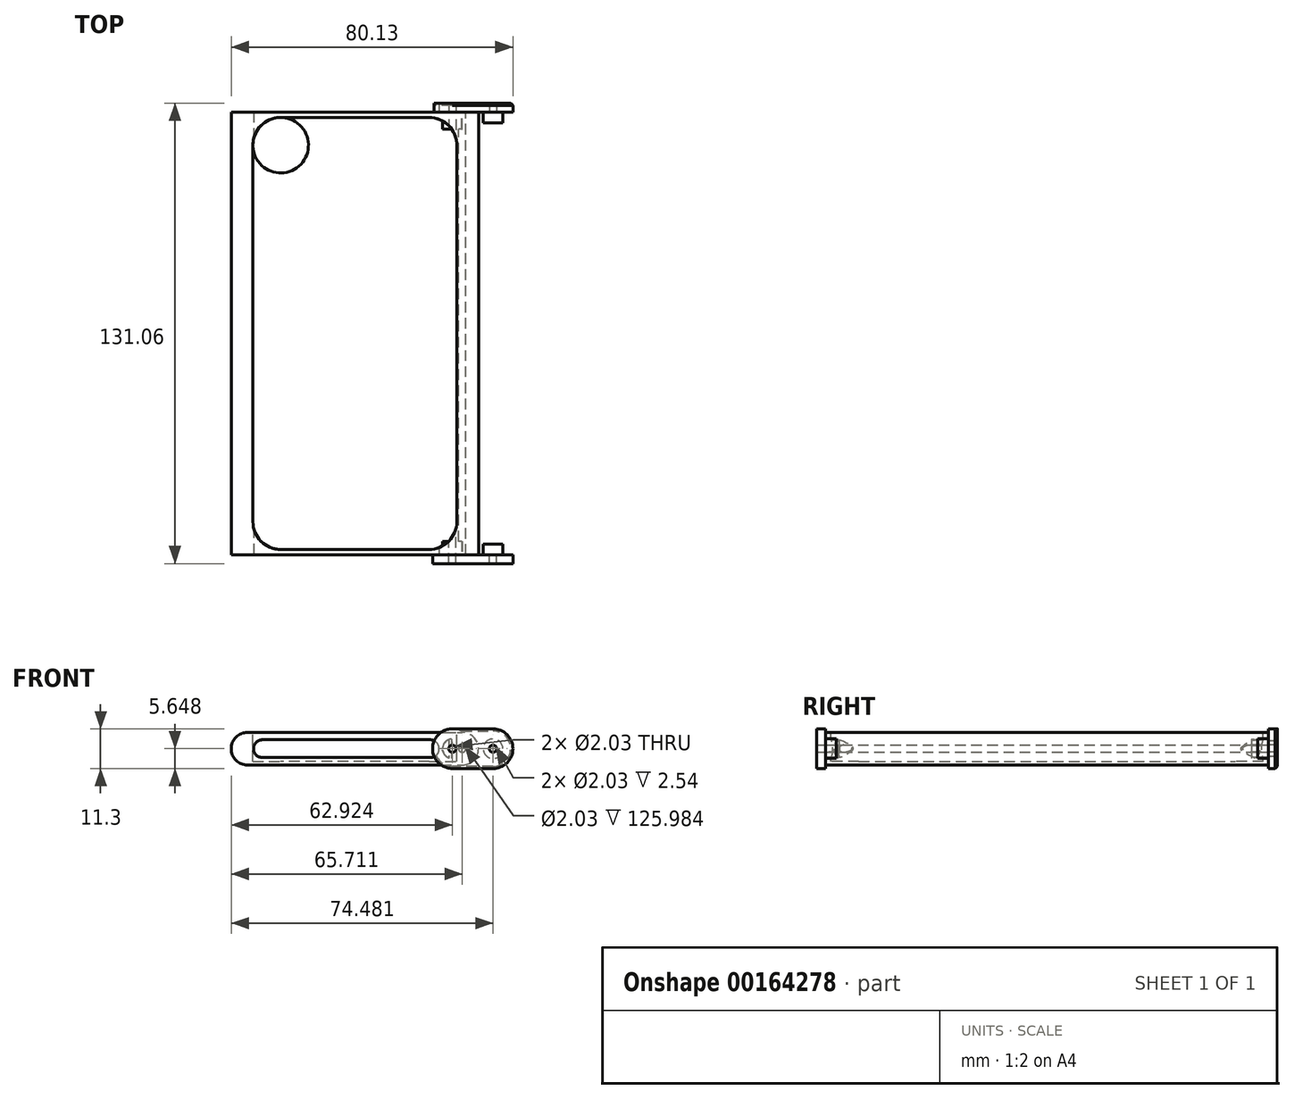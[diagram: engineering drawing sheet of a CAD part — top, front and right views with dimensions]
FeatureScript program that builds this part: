
annotation { "Feature Type Name" : "Feature", "Feature Type Description" : "" }
export const myFeature = defineFeature(function(context is Context, id is Id, definition is map)
    precondition{}
    {
        {
            var Q0;
            Q0=qCreatedBy(makeId("Top.planeOp"),FACE);
            var sketch = newSketch(context, id + "F0", { "sketchPlane" : qUnion([Q0])});
            skLineSegment(sketch, "E0.bottom", {"start": v(-35.18, 63) * mm, "end": v(35.18, 63) * mm});
            skLineSegment(sketch, "E0.top", {"start": v(-35.18, -63) * mm, "end": v(35.18, -63) * mm});
            skLineSegment(sketch, "E0.left", {"start": v(-35.18, 63) * mm, "end": v(-35.18, -63) * mm});
            skLineSegment(sketch, "E0.right", {"start": v(35.18, 63) * mm, "end": v(35.18, -63) * mm});
            skSolve(sketch);
        }
        {
            var Q0;
            Q0 = qSketchRegion(id + "F0", true);
            extrude(context, id + "F1", {"entities" : qUnion([Q0]), "depth" : 9.3 * mm});
        }
        {
            var Q0;
            Q0=makeQuery(id+"F1.opExtrude","CAP_FACE",FACE,{"disambiguationData":[OSD([sQuery(id+"F0.wireOp",EDGE,"E0.bottom"),sQuery(id+"F0.wireOp",EDGE,"E0.top"),sQuery(id+"F0.wireOp",EDGE,"E0.left"),sQuery(id+"F0.wireOp",EDGE,"E0.right")])],"isStart":false});
            var sketch = newSketch(context, id + "F2", { "sketchPlane" : qUnion([Q0])});
            skLineSegment(sketch, "E1.0", {"start": v(29, 61.47) * mm, "end": v(-29, 61.47) * mm});
            skLineSegment(sketch, "E1.1", {"start": v(29, -61.47) * mm, "end": v(29, 61.47) * mm});
            skLineSegment(sketch, "E1.2", {"start": v(-29, -61.47) * mm, "end": v(29, -61.47) * mm});
            skLineSegment(sketch, "E1.3", {"start": v(-29, 61.47) * mm, "end": v(-29, -61.47) * mm});
            skSolve(sketch);
        }
        {
            var Q0;
            Q0 = qSketchRegion(id + "F2", true);
            extrude(context, id + "F3", {"entities" : qUnion([Q0]), "operationType" : NewBodyOperationType.REMOVE, "oppositeDirection" : true, "depth" : 8.28 * mm});
        }
        {
            var Q0;
            Q0=makeQuery(id+"F3.boolean.opBoolean","COPY",EDGE,{"derivedFrom":makeQuery(id+"F3.opExtrude","SWEPT_EDGE",EDGE,{"disambiguationData":[OSD([sQuery(id+"F2.wireOp",EDGE,"E1.0"),sQuery(id+"F2.wireOp",EDGE,"E1.1")])]})});
            var Q1;
            Q1=makeQuery(id+"F3.boolean.opBoolean","COPY",EDGE,{"derivedFrom":makeQuery(id+"F3.opExtrude","SWEPT_EDGE",EDGE,{"disambiguationData":[OSD([sQuery(id+"F2.wireOp",EDGE,"E1.0"),sQuery(id+"F2.wireOp",EDGE,"E1.3")])]})});
            var Q2;
            Q2=makeQuery(id+"F3.boolean.opBoolean","COPY",EDGE,{"derivedFrom":makeQuery(id+"F3.opExtrude","SWEPT_EDGE",EDGE,{"disambiguationData":[OSD([sQuery(id+"F2.wireOp",EDGE,"E1.1"),sQuery(id+"F2.wireOp",EDGE,"E1.2")])]})});
            var Q3;
            Q3=makeQuery(id+"F3.boolean.opBoolean","COPY",EDGE,{"derivedFrom":makeQuery(id+"F3.opExtrude","SWEPT_EDGE",EDGE,{"disambiguationData":[OSD([sQuery(id+"F2.wireOp",EDGE,"E1.2"),sQuery(id+"F2.wireOp",EDGE,"E1.3")])]})});
            fillet(context, id + "F4", {"entities" : qUnion([Q0, Q1, Q2, Q3]), "radius" : 7.9 * mm, "tangentPropagation" : true, "allowEdgeOverflow" : false});
        }
        {
            var Q0;
            Q0=makeQuery(id+"F1.opExtrude","CAP_EDGE",EDGE,{"disambiguationData":[OSD([sQuery(id+"F0.wireOp",EDGE,"E0.left")])],"isStart":true});
            var Q1;
            Q1=makeQuery(id+"F1.opExtrude","CAP_EDGE",EDGE,{"disambiguationData":[OSD([sQuery(id+"F0.wireOp",EDGE,"E0.left")])],"isStart":false});
            var Q2;
            Q2=makeQuery(id+"F1.opExtrude","CAP_EDGE",EDGE,{"disambiguationData":[OSD([sQuery(id+"F0.wireOp",EDGE,"E0.right")])],"isStart":false});
            var Q3;
            Q3=makeQuery(id+"F1.opExtrude","CAP_EDGE",EDGE,{"disambiguationData":[OSD([sQuery(id+"F0.wireOp",EDGE,"E0.right")])],"isStart":true});
            fillet(context, id + "F5", {"entities" : qUnion([Q0, Q1, Q2, Q3]), "radius" : 4.65 * mm, "tangentPropagation" : true, "allowEdgeOverflow" : false});
        }
        {
            var Q0;
            Q0=makeQuery(id+"F1.opExtrude","SWEPT_FACE",FACE,{"disambiguationData":[OSD([sQuery(id+"F0.wireOp",EDGE,"E0.bottom")])]});
            var sketch = newSketch(context, id + "F6", { "sketchPlane" : qUnion([Q0])});
            skCircle(sketch, "E2", {"center": v(-30.53, 4.65) * mm, "radius": 1.02 * mm});
            skSolve(sketch);
        }
        {
            var Q0;
            Q0 = qSketchRegion(id + "F6", true);
            extrude(context, id + "F7", {"entities" : qUnion([Q0]), "operationType" : NewBodyOperationType.REMOVE, "endBound" : BoundingType.THROUGH_ALL, "oppositeDirection" : true, "depth" : 25.4 * mm});
        }
        {
            var Q0;
            Q0=makeQuery(id+"F1.opExtrude","SWEPT_FACE",FACE,{"disambiguationData":[OSD([sQuery(id+"F0.wireOp",EDGE,"E0.bottom")])]});
            var sketch = newSketch(context, id + "F8", { "sketchPlane" : qUnion([Q0])});
            skArc(sketch, "E3", {"start": v(-27.74, -1) * mm, "mid": v(-22.1, 4.66) * mm, "end": v(-27.76, 10.3) * mm});
            skArc(sketch, "E4", {"start": v(-39.3, 10.3) * mm, "mid": v(-44.95, 4.65) * mm, "end": v(-39.3, -1) * mm});
            skLineSegment(sketch, "E5", {"start": v(-39.3, 10.3) * mm, "end": v(-27.73, 10.3) * mm});
            skLineSegment(sketch, "E6", {"start": v(-39.3, -1) * mm, "end": v(-27.74, -1) * mm});
            skCircle(sketch, "E7", {"center": v(-39.3, 4.65) * mm, "radius": 1.02 * mm});
            skCircle(sketch, "E8", {"center": v(-27.74, 4.65) * mm, "radius": 1.02 * mm});
            skLineSegment(sketch, "E9", {"start": v(-27.74, 4.65) * mm, "end": v(-27.74, 10.3) * mm, "construction": true});
            skPoint(sketch, "E9.endSnap0", {"position": v(-33.51, 10.3) * mm});
            skLineSegment(sketch, "E10", {"start": v(-27.74, 10.3) * mm, "end": v(-27.74, -1) * mm, "construction": true});
            skSolve(sketch);
        }
        {
            var Q0;
            Q0 = qSketchRegion(id + "F8", true);
            extrude(context, id + "F9", {"entities" : qUnion([Q0]), "depth" : 2.54 * mm});
        }
        {
            var Q0;
            Q0=makeQuery(id+"F9.opExtrude","CAP_FACE",FACE,{"disambiguationData":[OSD([sQuery(id+"F8.wireOp",EDGE,"E3"),sQuery(id+"F8.wireOp",EDGE,"E4"),sQuery(id+"F8.wireOp",EDGE,"E5"),sQuery(id+"F8.wireOp",EDGE,"E6"),sQuery(id+"F8.wireOp",EDGE,"E7"),sQuery(id+"F8.wireOp",EDGE,"E8")])],"isStart":true});
            var sketch = newSketch(context, id + "F10", { "sketchPlane" : qUnion([Q0])});
            skCircle(sketch, "E11", {"center": v(39.3, 4.65) * mm, "radius": 2.8 * mm});
            skSolve(sketch);
        }
        {
            var Q0;
            Q0 = qSketchRegion(id + "F10", true);
            extrude(context, id + "F11", {"entities" : qUnion([Q0]), "operationType" : NewBodyOperationType.ADD, "depth" : 3.05 * mm});
        }
        {
            var Q0;
            Q0=makeQuery(id+"F9.opExtrude","SWEPT_BODY",BODY,{"disambiguationData":[OSD([sQuery(id+"F8.wireOp",EDGE,"E3"),sQuery(id+"F8.wireOp",EDGE,"E4"),sQuery(id+"F8.wireOp",EDGE,"E5"),sQuery(id+"F8.wireOp",EDGE,"E6"),sQuery(id+"F8.wireOp",EDGE,"E7")])]});
            var Q1;
            Q1=qCreatedBy(makeId("Front.planeOp"),FACE);
            mirror(context, id + "F12", {"entities" : qUnion([Q0]), "mirrorPlane" : qUnion([Q1])});
        }
        {
            var Q0;
            Q0=makeQuery(id+"F1.opExtrude","SWEPT_FACE",FACE,{"disambiguationData":[OSD([sQuery(id+"F0.wireOp",EDGE,"E0.top")])]});
            var sketch = newSketch(context, id + "F13", { "sketchPlane" : qUnion([Q0])});
            skArc(sketch, "E12", {"start": v(-26.3, 7.19) * mm, "mid": v(-28.84, 4.65) * mm, "end": v(-26.3, 2.1) * mm});
            skArc(sketch, "E13", {"start": v(21.44, 2.1) * mm, "mid": v(23.98, 4.65) * mm, "end": v(21.44, 7.19) * mm});
            skLineSegment(sketch, "E14", {"start": v(-26.3, 7.19) * mm, "end": v(21.44, 7.19) * mm});
            skLineSegment(sketch, "E15", {"start": v(-26.3, 2.1) * mm, "end": v(21.44, 2.1) * mm});
            skLineSegment(sketch, "E16", {"start": v(-35.18, 4.65) * mm, "end": v(8.12, 4.65) * mm, "construction": true});
            skSolve(sketch);
        }
        {
            var Q0;
            Q0 = qSketchRegion(id + "F13", true);
            extrude(context, id + "F14", {"entities" : qUnion([Q0]), "operationType" : NewBodyOperationType.REMOVE, "endBound" : BoundingType.THROUGH_ALL, "oppositeDirection" : true, "depth" : 25.4 * mm});
        }
        {
            var Q0;
            Q0=makeQuery(id+"F9.opExtrude","CAP_FACE",FACE,{"disambiguationData":[OSD([sQuery(id+"F8.wireOp",EDGE,"E3"),sQuery(id+"F8.wireOp",EDGE,"E4"),sQuery(id+"F8.wireOp",EDGE,"E5"),sQuery(id+"F8.wireOp",EDGE,"E6"),sQuery(id+"F8.wireOp",EDGE,"E7"),sQuery(id+"F8.wireOp",EDGE,"E8")])],"isStart":true});
            var sketch = newSketch(context, id + "F15", { "sketchPlane" : qUnion([Q0])});
            skCircle(sketch, "E17", {"center": v(27.74, 4.65) * mm, "radius": 2.8 * mm});
            skSolve(sketch);
        }
        {
            var Q0;
            Q0 = qSketchRegion(id + "F15", true);
            extrude(context, id + "F16", {"entities" : qUnion([Q0]), "operationType" : NewBodyOperationType.ADD, "depth" : 4.83 * mm});
        }
        {
            var Q0;
            Q0=makeQuery(id+"F12.opPattern","COPY",FACE,{"derivedFrom":makeQuery(id+"F9.opExtrude","CAP_FACE",FACE,{"disambiguationData":[OSD([sQuery(id+"F8.wireOp",EDGE,"E3"),sQuery(id+"F8.wireOp",EDGE,"E4"),sQuery(id+"F8.wireOp",EDGE,"E5"),sQuery(id+"F8.wireOp",EDGE,"E6"),sQuery(id+"F8.wireOp",EDGE,"E7"),sQuery(id+"F8.wireOp",EDGE,"E8")])],"isStart":true}),"instanceName":"1"});
            var sketch = newSketch(context, id + "F17", { "sketchPlane" : qUnion([Q0])});
            skCircle(sketch, "E18", {"center": v(-27.74, 4.65) * mm, "radius": 2.8 * mm});
            skSolve(sketch);
        }
        {
            var Q0;
            Q0 = qSketchRegion(id + "F17", true);
            extrude(context, id + "F18", {"entities" : qUnion([Q0]), "operationType" : NewBodyOperationType.ADD, "depth" : 3.8 * mm});
        }
        {
            var Q0;
            Q0=makeQuery(id+"F9.opExtrude","CAP_FACE",FACE,{"disambiguationData":[OSD([sQuery(id+"F8.wireOp",EDGE,"E3"),sQuery(id+"F8.wireOp",EDGE,"E4"),sQuery(id+"F8.wireOp",EDGE,"E5"),sQuery(id+"F8.wireOp",EDGE,"E6"),sQuery(id+"F8.wireOp",EDGE,"E7"),sQuery(id+"F8.wireOp",EDGE,"E8")])],"isStart":false});
            var sketch = newSketch(context, id + "F19", { "sketchPlane" : qUnion([Q0])});
            skCircle(sketch, "E19", {"center": v(-27.74, 4.65) * mm, "radius": 1.02 * mm});
            skSolve(sketch);
        }
        {
            var Q0;
            Q0 = qSketchRegion(id + "F19", true);
            extrude(context, id + "F20", {"entities" : qUnion([Q0]), "operationType" : NewBodyOperationType.REMOVE, "endBound" : BoundingType.THROUGH_ALL, "oppositeDirection" : true, "depth" : 25.4 * mm});
        }
        {
            var Q0;
            Q0=makeQuery(id+"F9.opExtrude","CAP_EDGE",EDGE,{"disambiguationData":[OSD([sQuery(id+"F8.wireOp",EDGE,"E5")])],"isStart":false});
            chamfer(context, id + "F21", {"entities" : qUnion([Q0]), "width" : 0.64 * mm, "tangentPropagation" : true});
        }
    });
